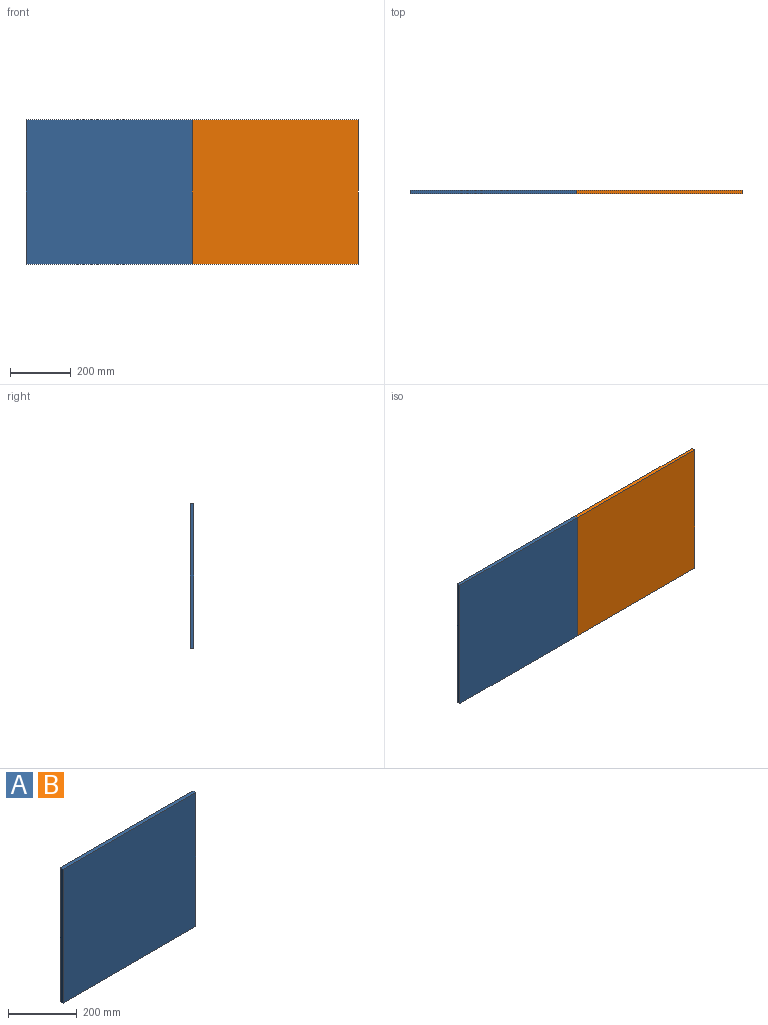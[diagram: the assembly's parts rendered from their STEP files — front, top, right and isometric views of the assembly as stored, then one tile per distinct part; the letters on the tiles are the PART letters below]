
ASSEMBLY  parts=2 mates=1
PART A: 6 faces, bbox 546.1x11.9x476.3 mm
  f0: plane 476.25x11.91mm, normal (-1,0,0), area 5670.4mm2, adj f1,f3,f4,f5
  f1: plane 546.1x11.91mm, normal (0,0,-1), area 6502mm2, adj f0,f2,f4,f5
  f2: plane 476.25x11.91mm, normal (1,0,0), area 5670.4mm2, adj f1,f3,f4,f5
  f3: plane 546.1x11.91mm, normal (0,0,1), area 6502mm2, adj f0,f2,f4,f5
  f4: plane 546.1x476.25mm, normal (0,-1,0), area 260080.1mm2, adj f0,f1,f2,f3
  f5: plane 546.1x476.25mm, normal (0,1,0), area 260080.1mm2, adj f0,f1,f2,f3
PART B: same geometry as A
PLACE A t=(-79.5,-34.7,-16.49)mm
PLACE B t=(466.6,-34.7,-16.49)mm
MATE fastened A.f4 <-> B.f4  axis (0,-1,0) through (255.15,-46.6,3.27)mm
